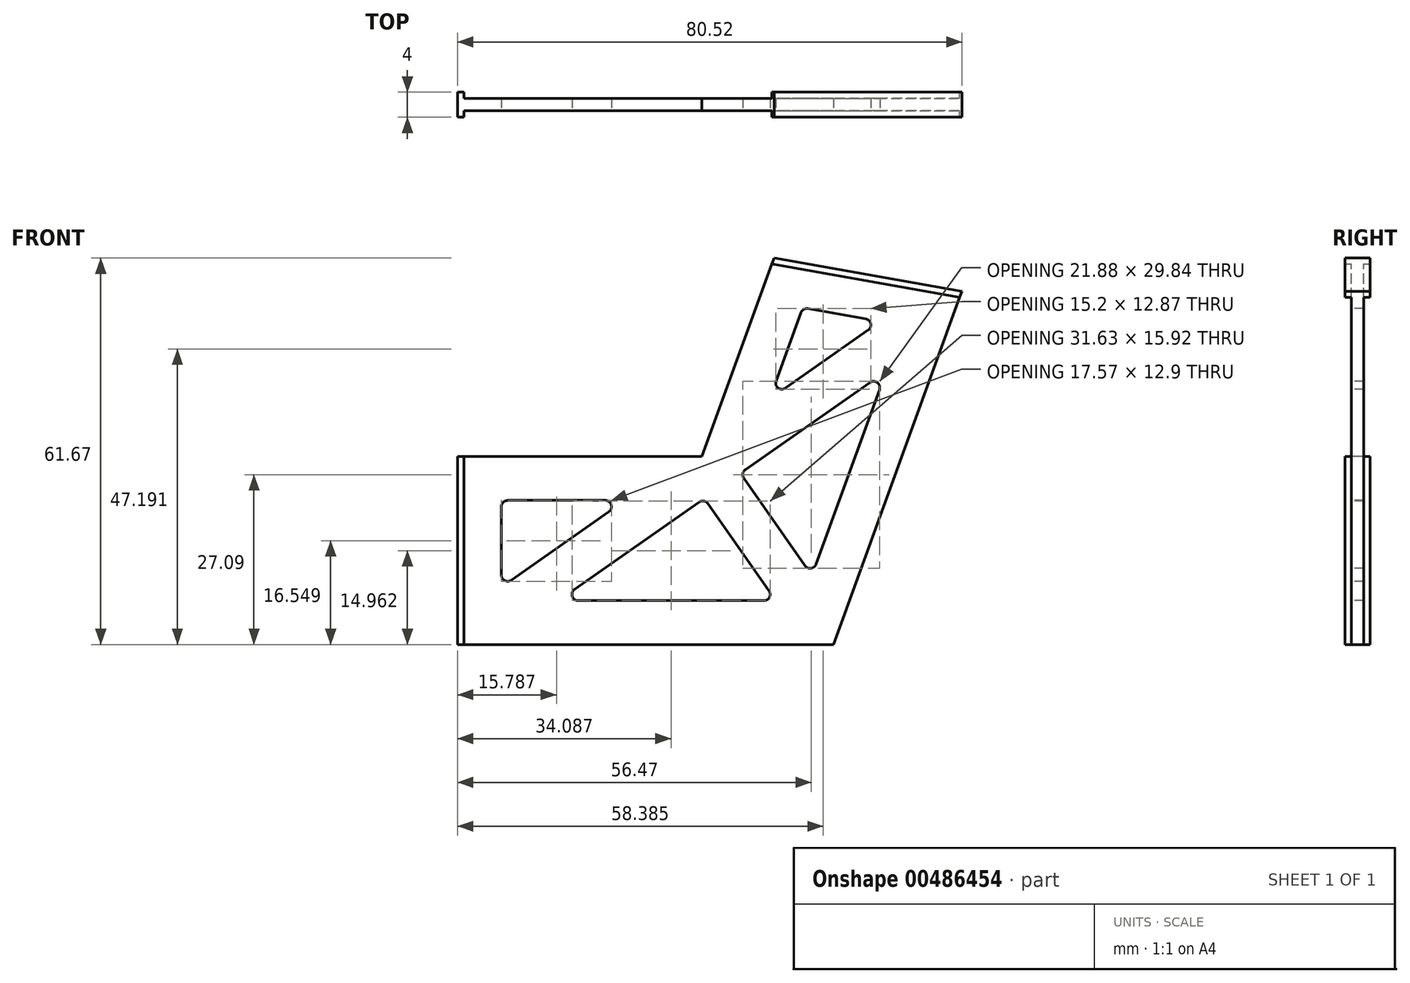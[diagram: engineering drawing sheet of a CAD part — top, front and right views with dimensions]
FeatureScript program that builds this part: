
annotation { "Feature Type Name" : "Feature", "Feature Type Description" : "" }
export const myFeature = defineFeature(function(context is Context, id is Id, definition is map)
    precondition{}
    {
        {
            var Q0;
            Q0=qCreatedBy(makeId("Front.planeOp"),FACE);
            var sketch = newSketch(context, id + "F0", { "sketchPlane" : qUnion([Q0])});
            skLineSegment(sketch, "E0", {"start": v(0, 0) * mm, "end": v(0, 0) * mm});
            skLineSegment(sketch, "E1", {"start": v(50, -65) * mm, "end": v(70.52, -8.63) * mm});
            skLineSegment(sketch, "E2", {"start": v(40.52, -3.34) * mm, "end": v(70.52, -8.63) * mm});
            skLineSegment(sketch, "E3", {"start": v(50, -65) * mm, "end": v(-10, -65) * mm});
            skLineSegment(sketch, "E4", {"start": v(-10, -65) * mm, "end": v(-10, -35) * mm});
            skLineSegment(sketch, "E5.0", {"start": v(29, -35) * mm, "end": v(40.52, -3.34) * mm});
            skLineSegment(sketch, "E6", {"start": v(-10, -35) * mm, "end": v(29, -35) * mm});
            skLineSegment(sketch, "E7.0", {"start": v(40.17, -4.3) * mm, "end": v(70.17, -9.58) * mm});
            skLineSegment(sketch, "E8.0", {"start": v(-9, -65) * mm, "end": v(-9, -35) * mm});
            skLineSegment(sketch, "E9.0", {"start": v(40.85, -22.91) * mm, "end": v(44.8, -12.04) * mm});
            skLineSegment(sketch, "E9.1", {"start": v(47.22, -52.19) * mm, "end": v(57.35, -24.34) * mm});
            skLineSegment(sketch, "E9.2", {"start": v(38.9, -58) * mm, "end": v(9.27, -58) * mm});
            skLineSegment(sketch, "E9.3", {"start": v(45.92, -11.4) * mm, "end": v(55.16, -13.03) * mm});
            skLineSegment(sketch, "E9.4", {"start": v(-3, -53.91) * mm, "end": v(-3, -43) * mm});
            skLineSegment(sketch, "E9.5", {"start": v(-2, -42) * mm, "end": v(13.57, -42) * mm});
            skLineSegment(sketch, "E10.0.left", {"start": v(-1.43, -54.73) * mm, "end": v(14.15, -43.83) * mm});
            skLineSegment(sketch, "E10.0.right", {"start": v(8.7, -56.2) * mm, "end": v(28.58, -42.27) * mm});
            skLineSegment(sketch, "E11.trimOffspring", {"start": v(42.36, -24.07) * mm, "end": v(55.56, -14.83) * mm});
            skLineSegment(sketch, "E12.0.left", {"start": v(35.7, -38.5) * mm, "end": v(45.46, -52.42) * mm});
            skLineSegment(sketch, "E12.0.right", {"start": v(29.97, -42.51) * mm, "end": v(39.72, -56.44) * mm});
            skLineSegment(sketch, "E13.trimOffspring", {"start": v(35.95, -37.1) * mm, "end": v(55.84, -23.18) * mm});
            skPoint(sketch, "E14.visualSharp", {"position": v(-3, -55.84) * mm});
            skArc(sketch, "E14.filletArc", {"start": v(-3, -53.91) * mm, "mid": v(-2.46, -54.8) * mm, "end": v(-1.43, -54.73) * mm});
            skPoint(sketch, "E15.visualSharp", {"position": v(-3, -42) * mm});
            skArc(sketch, "E15.filletArc", {"start": v(-2, -42) * mm, "mid": v(-2.7, -42.3) * mm, "end": v(-3, -43) * mm});
            skPoint(sketch, "E16.visualSharp", {"position": v(16.75, -42) * mm});
            skArc(sketch, "E16.filletArc", {"start": v(14.15, -43.83) * mm, "mid": v(14.53, -42.7) * mm, "end": v(13.57, -42) * mm});
            skPoint(sketch, "E17.visualSharp", {"position": v(29.4, -41.7) * mm});
            skArc(sketch, "E17.filletArc", {"start": v(29.97, -42.51) * mm, "mid": v(29.33, -42.1) * mm, "end": v(28.58, -42.27) * mm});
            skPoint(sketch, "E18.visualSharp", {"position": v(6.1, -58) * mm});
            skArc(sketch, "E18.filletArc", {"start": v(8.7, -56.2) * mm, "mid": v(8.32, -57.31) * mm, "end": v(9.27, -58) * mm});
            skPoint(sketch, "E19.visualSharp", {"position": v(40.83, -58) * mm});
            skArc(sketch, "E19.filletArc", {"start": v(38.9, -58) * mm, "mid": v(39.8, -57.47) * mm, "end": v(39.72, -56.44) * mm});
            skPoint(sketch, "E20.visualSharp", {"position": v(46.56, -54) * mm});
            skArc(sketch, "E20.filletArc", {"start": v(45.46, -52.42) * mm, "mid": v(46.4, -52.84) * mm, "end": v(47.22, -52.19) * mm});
            skPoint(sketch, "E21.visualSharp", {"position": v(35.14, -37.68) * mm});
            skArc(sketch, "E21.filletArc", {"start": v(35.95, -37.1) * mm, "mid": v(35.54, -37.75) * mm, "end": v(35.7, -38.5) * mm});
            skPoint(sketch, "E22.visualSharp", {"position": v(58.44, -21.36) * mm});
            skArc(sketch, "E22.filletArc", {"start": v(57.35, -24.34) * mm, "mid": v(57.02, -23.2) * mm, "end": v(55.84, -23.18) * mm});
            skPoint(sketch, "E23.visualSharp", {"position": v(45.1, -11.25) * mm});
            skArc(sketch, "E23.filletArc", {"start": v(45.92, -11.4) * mm, "mid": v(45.24, -11.52) * mm, "end": v(44.8, -12.04) * mm});
            skPoint(sketch, "E24.visualSharp", {"position": v(39.76, -25.9) * mm});
            skArc(sketch, "E24.filletArc", {"start": v(40.85, -22.91) * mm, "mid": v(41.18, -24.05) * mm, "end": v(42.36, -24.07) * mm});
            skPoint(sketch, "E25.visualSharp", {"position": v(57.54, -13.45) * mm});
            skArc(sketch, "E25.filletArc", {"start": v(55.56, -14.83) * mm, "mid": v(55.96, -13.8) * mm, "end": v(55.16, -13.03) * mm});
            skSolve(sketch);
        }
        {
            var Q0;
            Q0=qSketchRegion(id+"F0",true);
            extrude(context, id + "F1", {"entities" : qUnion([Q0]), "endBound" : BoundingType.SYMMETRIC, "oppositeDirection" : true, "depth" : 2 * mm, "offsetDistance" : 25 * mm});
        }
        {
            var Q0;
            {var subQ0=sQuery(id+"F0.wireOp",EDGE,"E2");Q0=makeQuery(id+"F0.imprint","IMPRINT",FACE,{"disambiguationData":[TD([[makeQuery(id+"F0.imprint","IMPRINT",EDGE,{"derivedFrom":subQ0}),-1.0]])]});}
            var Q1;
            {var subQ0=sQuery(id+"F0.wireOp",EDGE,"E4");Q1=makeQuery(id+"F0.imprint","IMPRINT",FACE,{"disambiguationData":[TD([[makeQuery(id+"F0.imprint","IMPRINT",EDGE,{"derivedFrom":subQ0}),-1.0]])]});}
            extrude(context, id + "F2", {"entities" : qUnion([Q0, Q1]), "operationType" : NewBodyOperationType.ADD, "endBound" : BoundingType.SYMMETRIC, "depth" : 4 * mm, "offsetDistance" : 25 * mm});
        }
    });
